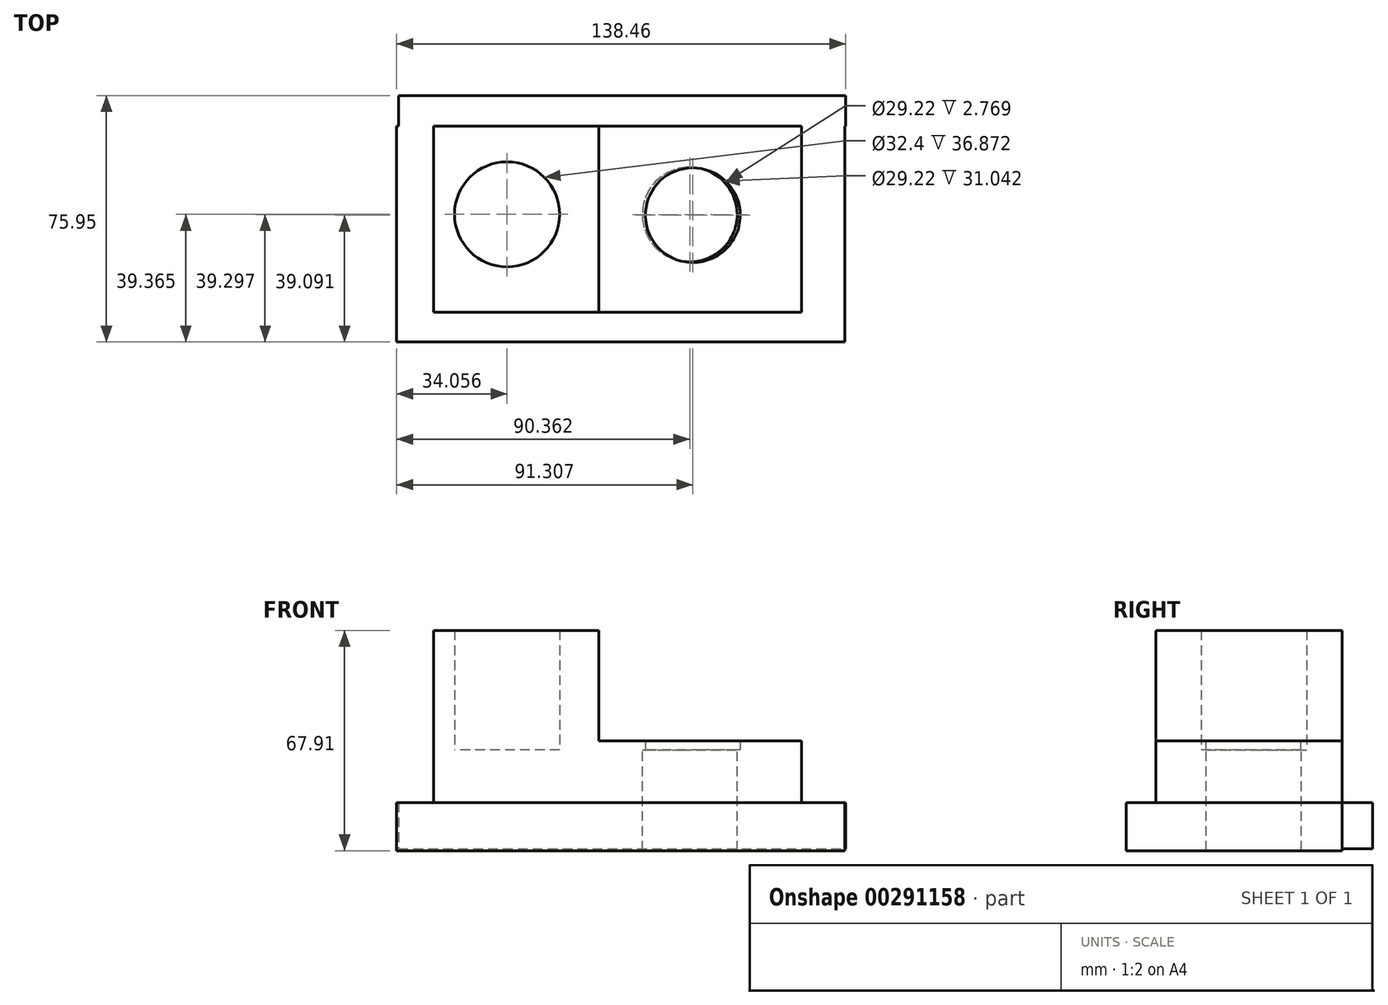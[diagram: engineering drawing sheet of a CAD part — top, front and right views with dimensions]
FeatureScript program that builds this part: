
annotation { "Feature Type Name" : "Feature", "Feature Type Description" : "" }
export const myFeature = defineFeature(function(context is Context, id is Id, definition is map)
    precondition{}
    {
        {
            var Q0;
            Q0=qCreatedBy(makeId("Front.planeOp"),FACE);
            var sketch = newSketch(context, id + "F0", { "sketchPlane" : qUnion([Q0])});
            skLineSegment(sketch, "E0", {"start": v(-64.7, 36.87) * mm, "end": v(-64.7, -22.88) * mm});
            skLineSegment(sketch, "E1", {"start": v(48.68, -22.88) * mm, "end": v(-64.7, -22.88) * mm});
            skLineSegment(sketch, "E2", {"start": v(-13.7, 36.87) * mm, "end": v(-64.7, 36.87) * mm});
            skLineSegment(sketch, "E3", {"start": v(-13.7, 36.87) * mm, "end": v(-13.7, 2.77) * mm});
            skLineSegment(sketch, "E4", {"start": v(-13.7, 2.77) * mm, "end": v(48.68, 2.77) * mm});
            skLineSegment(sketch, "E5", {"start": v(48.68, 2.77) * mm, "end": v(48.68, -22.88) * mm});
            skSolve(sketch);
        }
        {
            var Q0;
            Q0 = qSketchRegion(id + "F0", true);
            extrude(context, id + "F1", {"entities" : qUnion([Q0]), "depth" : 57.4 * mm});
        }
        {
            var Q0;
            Q0=qCreatedBy(makeId("Front.planeOp"),FACE);
            var sketch = newSketch(context, id + "F2", { "sketchPlane" : qUnion([Q0])});
            skLineSegment(sketch, "E6", {"start": v(62.08, -16.18) * mm, "end": v(-76.08, -16.18) * mm});
            skLineSegment(sketch, "E7", {"start": v(-76.08, -16.18) * mm, "end": v(-76.08, -31.04) * mm});
            skLineSegment(sketch, "E8", {"start": v(-76.08, -31.04) * mm, "end": v(62.08, -31.04) * mm});
            skLineSegment(sketch, "E9", {"start": v(62.08, -31.04) * mm, "end": v(62.08, -16.18) * mm});
            skSolve(sketch);
        }
        {
            var Q0;
            Q0 = qSketchRegion(id + "F2", true);
            extrude(context, id + "F3", {"entities" : qUnion([Q0]), "operationType" : NewBodyOperationType.ADD, "depth" : 66.55 * mm});
        }
        {
            var Q0;
            Q0=qCreatedBy(makeId("Front.planeOp"),FACE);
            var sketch = newSketch(context, id + "F4", { "sketchPlane" : qUnion([Q0])});
            skLineSegment(sketch, "E10", {"start": v(62.38, -16.18) * mm, "end": v(-75.5, -16.18) * mm});
            skLineSegment(sketch, "E11", {"start": v(-75.5, -16.18) * mm, "end": v(-75.5, -30.46) * mm});
            skLineSegment(sketch, "E12", {"start": v(-75.5, -30.46) * mm, "end": v(62.38, -30.46) * mm});
            skLineSegment(sketch, "E13", {"start": v(62.38, -30.46) * mm, "end": v(62.38, -16.18) * mm});
            skSolve(sketch);
        }
        {
            var Q0;
            Q0 = qSketchRegion(id + "F4", true);
            extrude(context, id + "F5", {"entities" : qUnion([Q0]), "operationType" : NewBodyOperationType.ADD, "oppositeDirection" : true, "depth" : 9.4 * mm});
        }
        {
            var Q0;
            Q0=qCreatedBy(makeId("Top.planeOp"),FACE);
            var sketch = newSketch(context, id + "F6", { "sketchPlane" : qUnion([Q0])});
            skCircle(sketch, "E14", {"center": v(-42.02, -27.18) * mm, "radius": 16.2 * mm});
            skCircle(sketch, "E15", {"center": v(15.23, -27.46) * mm, "radius": 14.61 * mm});
            skSolve(sketch);
        }
        {
            var Q0;
            Q0 = qSketchRegion(id + "F6", true);
            extrude(context, id + "F7", {"entities" : qUnion([Q0]), "operationType" : NewBodyOperationType.REMOVE, "depth" : 62.48 * mm});
        }
        {
            var Q0;
            Q0=qCreatedBy(makeId("Top.planeOp"),FACE);
            var sketch = newSketch(context, id + "F8", { "sketchPlane" : qUnion([Q0])});
            skCircle(sketch, "E16", {"center": v(14.28, -27.25) * mm, "radius": 14.61 * mm});
            skSolve(sketch);
        }
        {
            var Q0;
            Q0 = qSketchRegion(id + "F8", true);
            extrude(context, id + "F9", {"entities" : qUnion([Q0]), "operationType" : NewBodyOperationType.REMOVE, "oppositeDirection" : true, "depth" : 50.3 * mm});
        }
        {
            var Q0;
            Q0 = qSketchRegion(id + "F8", true);
            extrude(context, id + "F10", {"entities" : qUnion([Q0]), "operationType" : NewBodyOperationType.REMOVE, "oppositeDirection" : true, "depth" : 41.4 * mm});
        }
    });
